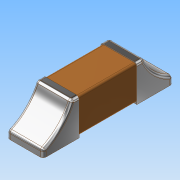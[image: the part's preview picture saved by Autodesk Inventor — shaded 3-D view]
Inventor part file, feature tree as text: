
AUTODESK INVENTOR PART (.ipt)
format: ipt  version: 2016 (Build 200138000, 138)  size: 194,048 bytes
history: native  units: mm
features: extrude x3, fillet x3, sketch x2, mirror x1, projected_geometry x1
ambient origin geometry x8: Origin, YZ Plane, XZ Plane, XY Plane, X Axis, Y Axis, Z Axis, Center Point
bodies: Body1 (feature_tree)
feature tree (10):
  extrude  "Extrusion4"  Depth=0.475mm
  sketch  "Sketch11"  dims[d9=0.475mm d10=0.0mm d11=0.5mm d12=0.1mm d13=0.0mm d14=0.1mm d15=0.5mm d16=0.0mm d17=0.75mm d18=0.0425mm d19=0.03mm]
  extrude  "Extrusion5"  Depth=0.5mm
  extrude  "Extrusion6"  Depth=0.03mm TaperAngle=0.0deg
  fillet  "Fillet1"  Radius=0.1mm
  fillet  "Fillet2"  Radius=0.5mm
  mirror  "Mirror1"
  fillet  "Fillet3"  Radius=0.75mm
  sketch  "Sketch10"  dims[d7=0.8mm d8=0.475mm]
  projected_geometry  "Projected Loop1"
